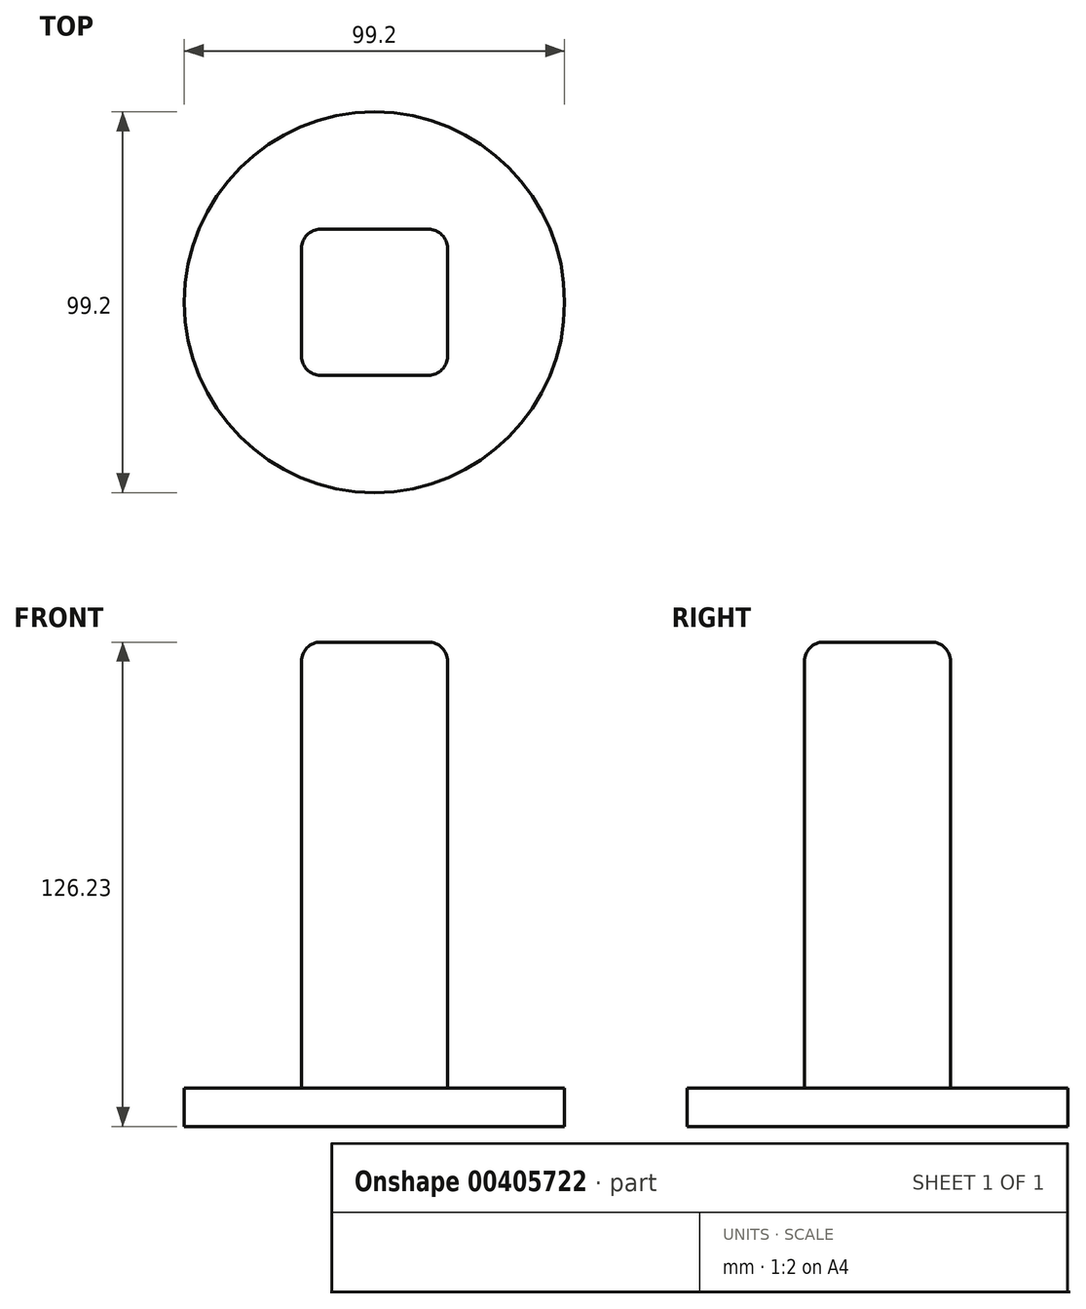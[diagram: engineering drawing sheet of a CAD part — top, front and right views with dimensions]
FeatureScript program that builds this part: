
annotation { "Feature Type Name" : "Feature", "Feature Type Description" : "" }
export const myFeature = defineFeature(function(context is Context, id is Id, definition is map)
    precondition{}
    {
        {
            var Q0;
            Q0=qCreatedBy(makeId("Front.planeOp"),FACE);
            var sketch = newSketch(context, id + "F0", { "sketchPlane" : qUnion([Q0])});
            skLineSegment(sketch, "E0", {"start": v(0, 230.97) * mm, "end": v(0, 240.97) * mm});
            skPoint(sketch, "E1.visualSharp", {"position": v(49.6, 240.97) * mm});
            skPoint(sketch, "E2.visualSharp", {"position": v(49.6, 230.97) * mm});
            skLineSegment(sketch, "E3", {"start": v(0, 240.97) * mm, "end": v(49.6, 240.97) * mm});
            skLineSegment(sketch, "E4", {"start": v(49.6, 230.97) * mm, "end": v(49.6, 240.97) * mm});
            skLineSegment(sketch, "E5", {"start": v(49.6, 230.97) * mm, "end": v(0, 230.97) * mm});
            skSolve(sketch);
        }
        {
            var Q0;
            Q0 = qSketchRegion(id + "F0", true);
            var Q1;
            Q1=sQuery(id+"F0.wireOp",EDGE,"E0");
            revolve(context, id + "F1", {"entities" : qUnion([Q0]), "axis" : qUnion([Q1]), "revolveType" : RevolveType.FULL});
        }
        {
            var Q0;
            Q0=makeQuery(id+"F1.opRevolve","SWEPT_FACE",FACE,{"disambiguationData":[OSD([sQuery(id+"F0.wireOp",EDGE,"E3")])]});
            var sketch = newSketch(context, id + "F2", { "sketchPlane" : qUnion([Q0])});
            skLineSegment(sketch, "E6.bottom", {"start": v(14.05, 19.05) * mm, "end": v(-14.05, 19.05) * mm});
            skLineSegment(sketch, "E6.top", {"start": v(14.05, -19.05) * mm, "end": v(-14.05, -19.05) * mm});
            skLineSegment(sketch, "E6.left", {"start": v(19.05, 14.05) * mm, "end": v(19.05, -14.05) * mm});
            skLineSegment(sketch, "E6.right", {"start": v(-19.05, 14.05) * mm, "end": v(-19.05, -14.05) * mm});
            skPoint(sketch, "E7.visualSharp", {"position": v(-19.05, 19.05) * mm});
            skArc(sketch, "E7.filletArc", {"start": v(-14.05, 19.05) * mm, "mid": v(-17.59, 17.59) * mm, "end": v(-19.05, 14.05) * mm});
            skPoint(sketch, "E8.visualSharp", {"position": v(19.05, 19.05) * mm});
            skArc(sketch, "E8.filletArc", {"start": v(19.05, 14.05) * mm, "mid": v(17.59, 17.59) * mm, "end": v(14.05, 19.05) * mm});
            skPoint(sketch, "E9.visualSharp", {"position": v(19.05, -19.05) * mm});
            skArc(sketch, "E9.filletArc", {"start": v(14.05, -19.05) * mm, "mid": v(17.59, -17.59) * mm, "end": v(19.05, -14.05) * mm});
            skPoint(sketch, "E10.visualSharp", {"position": v(-19.05, -19.05) * mm});
            skArc(sketch, "E10.filletArc", {"start": v(-19.05, -14.05) * mm, "mid": v(-17.59, -17.59) * mm, "end": v(-14.05, -19.05) * mm});
            skSolve(sketch);
        }
        {
            var Q0;
            Q0=makeQuery(id+"F2.imprint","IMPRINT",FACE,{"disambiguationData":[TD([[makeQuery(id+"F2.imprint","IMPRINT",EDGE,{"derivedFrom":sQuery(id+"F2.wireOp",EDGE,"E6.bottom")}),1.0]])]});
            extrude(context, id + "F3", {"entities" : qUnion([Q0]), "operationType" : NewBodyOperationType.ADD, "depth" : 116.23 * mm});
        }
        {
            var Q0;
            Q0=makeQuery(id+"F3.opExtrude","CAP_EDGE",EDGE,{"disambiguationData":[OSD([sQuery(id+"F2.wireOp",EDGE,"E6.top")])],"isStart":false});
            fillet(context, id + "F4", {"entities" : qUnion([Q0]), "radius" : 5 * mm, "tangentPropagation" : true, "allowEdgeOverflow" : false});
        }
    });
